FCSTD DOCUMENT  (FreeCAD 0.21R33771 (Git))
Label: assembly
License: All rights reserved
LicenseURL: https://en.wikipedia.org/wiki/All_rights_reserved
objects: App::FeaturePython×4, Part::FeaturePython×2, Part::Fuse×1, Mesh::Feature×1
note: 3 computed .brp shape members not serialized (recipe doc carries the construction recipe); baked Part::Feature solids carry a one-line shape summary decoded from their .brp

FEATURE [Part::FeaturePython] b_drift1_dipole_001_  label="drift1_dipole_001"  # a2plus imported part (geometry in sourceFile) (typed FeaturePython)
  a2p_Version = 0.4.65
  fixedPosition = true
  objectType = a2pPart
  sourceFile = ./drift1_dipole.FCStd
  subassemblyImport = false
  timeLastImport = 1.72297e+09
  updateColors = true
FEATURE [Part::FeaturePython] b_drift2_001_  label="drift2_001"  # a2plus imported part (geometry in sourceFile) (typed FeaturePython)
  Placement = pos=(-124.998,-2.244e-12,19999.4) rot=(0,-1,0;0.01rad)
  a2p_Version = 0.4.65
  fixedPosition = false
  objectType = a2pPart
  sourceFile = ./drift2.FCStd
  subassemblyImport = false
  timeLastImport = 1.72297e+09
  updateColors = true
FEATURE [App::FeaturePython] planeCoincident_001  label="planeCoincident_001__drift2_001"  # a2plus constraint (typed FeaturePython)
  Object1 = b_drift1_dipole_001_
  Object2 = b_drift2_001_
  ParentTreeObject = -> b_drift1_dipole_001_
  SubElement1 = Face14
  SubElement2 = Face17
  Suppressed = false
  Type = plane
  directionConstraint = 0
  offset = 0
FEATURE [App::FeaturePython] planeCoincident_001_mirror  label="planeCoincident_001__drift1_dipole_001"  # a2plus constraint (typed FeaturePython)
  Object1 = b_drift1_dipole_001_
  Object2 = b_drift2_001_
  ParentTreeObject = -> b_drift2_001_
  SubElement1 = Face14
  SubElement2 = Face17
  Suppressed = false
  Type = plane
  directionConstraint = 0
  offset = 0
FEATURE [App::FeaturePython] centerOfMass_001  label="centerOfMass_001__drift1_dipole_001"  # a2plus constraint (typed FeaturePython)
  Object1 = b_drift2_001_
  Object2 = b_drift1_dipole_001_
  ParentTreeObject = -> b_drift2_001_
  SubElement1 = Face17
  SubElement2 = Face14
  Suppressed = false
  Type = CenterOfMass
  directionConstraint = 0
  lockRotation = false
  offset = 0
FEATURE [App::FeaturePython] centerOfMass_001_mirror  label="centerOfMass_001__drift2_001"  # a2plus constraint (typed FeaturePython)
  Object1 = b_drift2_001_
  Object2 = b_drift1_dipole_001_
  ParentTreeObject = -> b_drift1_dipole_001_
  SubElement1 = Face17
  SubElement2 = Face14
  Suppressed = false
  Type = CenterOfMass
  directionConstraint = 0
  lockRotation = false
  offset = 0
FEATURE [Part::Fuse] Fusion
  Base = -> b_drift1_dipole_001_
  Tool = -> b_drift2_001_
FEATURE [Mesh::Feature] Mesh  label="Fusion (Meshed)"
